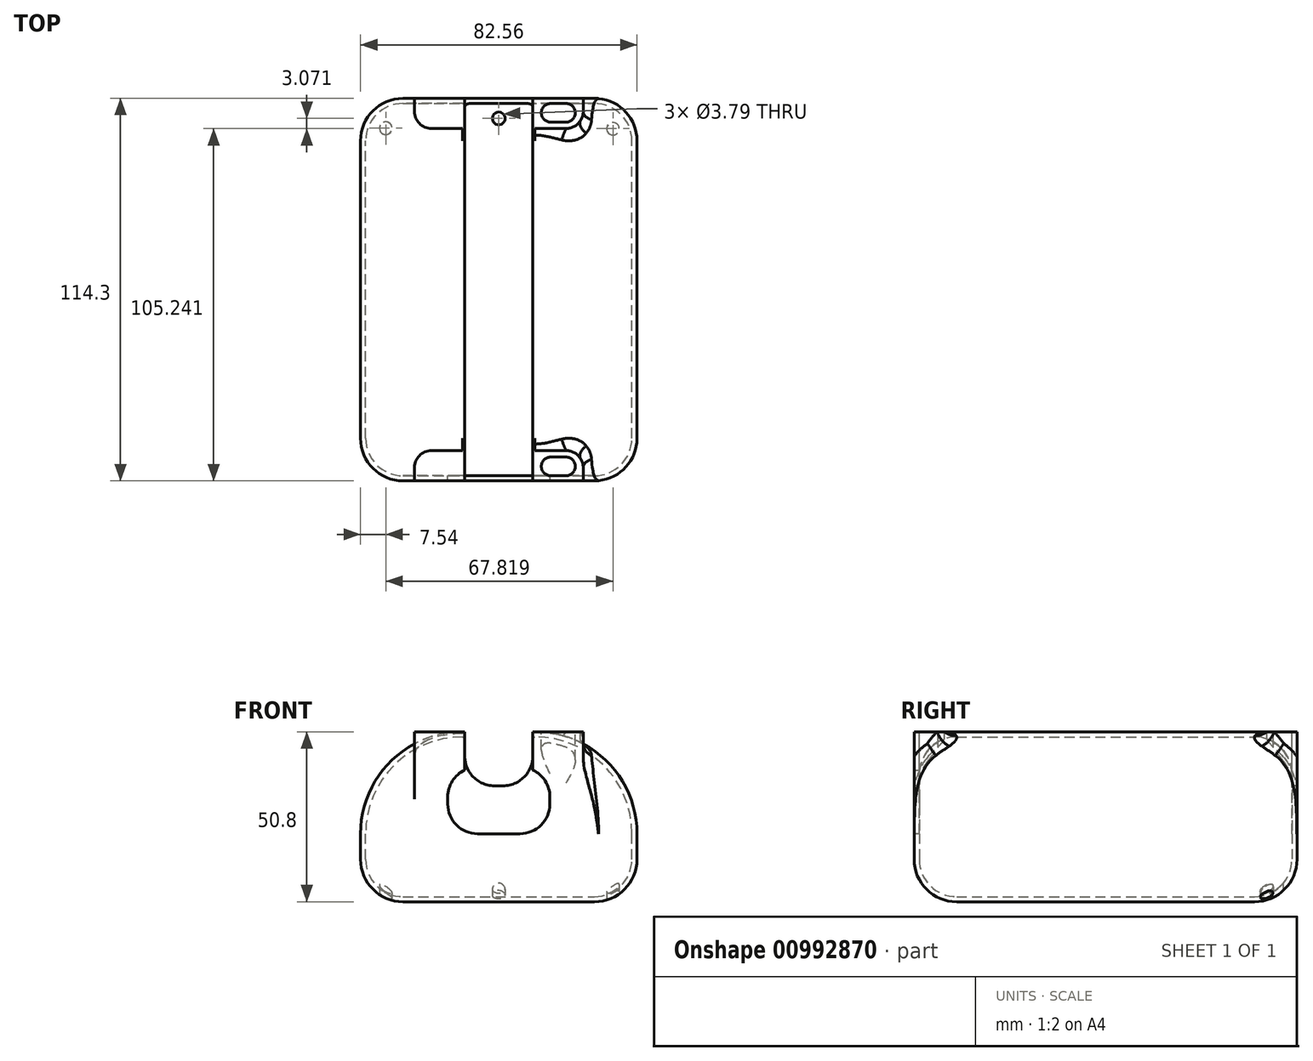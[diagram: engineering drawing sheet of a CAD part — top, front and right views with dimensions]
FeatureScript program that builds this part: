
annotation { "Feature Type Name" : "Feature", "Feature Type Description" : "" }
export const myFeature = defineFeature(function(context is Context, id is Id, definition is map)
    precondition{}
    {
        {
            var Q0;
            Q0=qCreatedBy(makeId("Top.planeOp"),FACE);
            var sketch = newSketch(context, id + "F0", { "sketchPlane" : qUnion([Q0])});
            skLineSegment(sketch, "E0.bottom", {"start": v(41.28, 0) * mm, "end": v(-41.28, 0) * mm});
            skLineSegment(sketch, "E0.top", {"start": v(41.28, 114.3) * mm, "end": v(-41.28, 114.3) * mm});
            skLineSegment(sketch, "E0.left", {"start": v(41.28, 0) * mm, "end": v(41.28, 114.3) * mm});
            skLineSegment(sketch, "E0.right", {"start": v(-41.28, 0) * mm, "end": v(-41.28, 114.3) * mm});
            skPoint(sketch, "E0.middle", {"position": v(0, 57.15) * mm});
            skSolve(sketch);
        }
        {
            var Q0;
            Q0=makeQuery(id+"F0.imprint","IMPRINT",FACE,{"disambiguationData":[TD([[makeQuery(id+"F0.imprint","IMPRINT",EDGE,{"derivedFrom":sQuery(id+"F0.wireOp",EDGE,"E0.bottom")}),-1.0]])]});
            extrude(context, id + "F1", {"entities" : qUnion([Q0]), "depth" : 50.8 * mm, "offsetDistance" : 25.4 * mm});
        }
        {
            var Q0;
            Q0=makeQuery(id+"F1.opExtrude","CAP_EDGE",EDGE,{"disambiguationData":[OSD([sQuery(id+"F0.wireOp",EDGE,"E0.left")])],"isStart":false});
            var Q1;
            Q1=makeQuery(id+"F1.opExtrude","CAP_EDGE",EDGE,{"disambiguationData":[OSD([sQuery(id+"F0.wireOp",EDGE,"E0.right")])],"isStart":false});
            fillet(context, id + "F2", {"entities" : qUnion([Q0, Q1]), "radius" : 30.48 * mm, "tangentPropagation" : true, "allowEdgeOverflow" : false});
        }
        {
            var Q0;
            Q0=makeQuery(id+"F1.opExtrude","SWEPT_FACE",FACE,{"disambiguationData":[OSD([sQuery(id+"F0.wireOp",EDGE,"E0.left")])]});
            var Q1;
            Q1=makeQuery(id+"F1.opExtrude","SWEPT_FACE",FACE,{"disambiguationData":[OSD([sQuery(id+"F0.wireOp",EDGE,"E0.right")])]});
            var Q2;
            Q2=makeQuery(id+"F1.opExtrude","CAP_EDGE",EDGE,{"disambiguationData":[OSD([sQuery(id+"F0.wireOp",EDGE,"E0.top")])],"isStart":true});
            var Q3;
            Q3=makeQuery(id+"F1.opExtrude","CAP_EDGE",EDGE,{"disambiguationData":[OSD([sQuery(id+"F0.wireOp",EDGE,"E0.bottom")])],"isStart":true});
            var Q4;
            Q4=makeQuery(id+"F1.opExtrude","CAP_EDGE",EDGE,{"disambiguationData":[OSD([sQuery(id+"F0.wireOp",EDGE,"E0.top")])],"isStart":false});
            fillet(context, id + "F3", {"entities" : qUnion([Q0, Q1, Q2, Q3, Q4]), "radius" : 12.7 * mm, "tangentPropagation" : true, "allowEdgeOverflow" : false});
        }
        {
            var Q0;
            {var subQ0=sQuery(id+"F0.wireOp",EDGE,"E0.right");var subQ1=sQuery(id+"F0.wireOp",EDGE,"E0.left");var subQ2=sQuery(id+"F0.wireOp",EDGE,"E0.top");var subQ3=sQuery(id+"F0.wireOp",EDGE,"E0.bottom");Q0=makeQuery(id+"F4FyCP3RIGp18HZ_1.splitOp","SPLIT_SURFACE_INTERSECT",FACE,{"derivedFrom":[makeQuery(id+"F3.opFillet","BLEND_FACE",FACE,{"disambiguationData":[OSD([subQ1]),TDD([makeQuery(id+"F1.opExtrude","CAP_EDGE",EDGE,{"disambiguationData":[OSD([subQ1])],"isStart":true})])]}),makeQuery(id+"F3.opFillet","BLEND_FACE",FACE,{"disambiguationData":[OSD([subQ1]),TDD([makeQuery(id+"F1.opExtrude","CAP_EDGE",EDGE,{"disambiguationData":[OSD([subQ1])],"isStart":false})])]}),makeQuery(id+"F3.opFillet","BLEND_FACE",FACE,{"disambiguationData":[OSD([subQ0]),TDD([makeQuery(id+"F1.opExtrude","CAP_EDGE",EDGE,{"disambiguationData":[OSD([subQ0])],"isStart":true})])]}),makeQuery(id+"F3.opFillet","BLEND_FACE",FACE,{"disambiguationData":[OSD([subQ0]),TDD([makeQuery(id+"F1.opExtrude","CAP_EDGE",EDGE,{"disambiguationData":[OSD([subQ0])],"isStart":false})])]}),makeQuery(id+"F1.opExtrude","CAP_FACE",FACE,{"disambiguationData":[OSD([subQ3,subQ2,subQ1,subQ0])],"isStart":true}),makeQuery(id+"F1.opExtrude","CAP_FACE",FACE,{"disambiguationData":[OSD([subQ3,subQ2,subQ1,subQ0])],"isStart":false}),makeQuery(id+"F1.opExtrude","SWEPT_FACE",FACE,{"disambiguationData":[OSD([subQ1])]}),makeQuery(id+"F1.opExtrude","SWEPT_FACE",FACE,{"disambiguationData":[OSD([subQ0])]})],"isFromBackBody":true});}
            var Q1;
            Q1=makeQuery(id+"F1.opExtrude","SWEPT_BODY",BODY,{"disambiguationData":[OSD([sQuery(id+"F0.wireOp",EDGE,"E0.bottom"),sQuery(id+"F0.wireOp",EDGE,"E0.top"),sQuery(id+"F0.wireOp",EDGE,"E0.left"),sQuery(id+"F0.wireOp",EDGE,"E0.right")])]});
            shell(context, id + "F4", {"isHollow" : true, "entities" : qUnion([Q0]), "parts" : qUnion([Q1]), "thickness" : 1.52 * mm});
        }
        {
            var Q0;
            Q0=makeQuery(id+"F4FyCP3RIGp18HZ_1.splitOp","SPLIT",FACE,{"derivedFrom":makeQuery(id+"F1.opExtrude","CAP_FACE",FACE,{"disambiguationData":[OSD([sQuery(id+"F0.wireOp",EDGE,"E0.bottom"),sQuery(id+"F0.wireOp",EDGE,"E0.top"),sQuery(id+"F0.wireOp",EDGE,"E0.left"),sQuery(id+"F0.wireOp",EDGE,"E0.right")])],"isStart":false}),"isFromBackBody":true});
            var sketch = newSketch(context, id + "F5", { "sketchPlane" : qUnion([Q0])});
            skLineSegment(sketch, "E1.bottom", {"start": v(12.7, 7.11) * mm, "end": v(22.86, 7.11) * mm});
            skLineSegment(sketch, "E1.top", {"start": v(12.7, 1.52) * mm, "end": v(22.86, 1.52) * mm});
            skLineSegment(sketch, "E1.left", {"start": v(12.7, 7.11) * mm, "end": v(12.7, 1.52) * mm});
            skLineSegment(sketch, "E1.right", {"start": v(22.86, 7.11) * mm, "end": v(22.86, 1.52) * mm});
            skSolve(sketch);
        }
        {
            var Q0;
            {var subQ0=sQuery(id+"F0.wireOp",EDGE,"E0.right");var subQ1=sQuery(id+"F0.wireOp",EDGE,"E0.left");var subQ2=sQuery(id+"F0.wireOp",EDGE,"E0.top");var subQ3=sQuery(id+"F0.wireOp",EDGE,"E0.bottom");var subQ4=makeQuery(id+"F1.opExtrude","CAP_FACE",FACE,{"disambiguationData":[OSD([subQ3,subQ2,subQ1,subQ0])],"isStart":false});var subQ5=subQ4;Q0=makeQuery(id+"F5.imprint","IMPRINT",FACE,{"disambiguationData":[TD([[makeQuery(id+"F5.imprint","IMPRINT",EDGE,{"derivedFrom":makeQuery(id+"F3.opFillet","BLEND_EDGE",EDGE,{"blendedFrom":[makeQuery(id+"F1.opExtrude","CAP_EDGE",EDGE,{"disambiguationData":[OSD([subQ3])],"isStart":false}),subQ5],"blendedInto":[subQ5]})}),1.0]])]});}
            var sketch = newSketch(context, id + "F6", { "sketchPlane" : qUnion([Q0])});
            skLineSegment(sketch, "E2.bottom", {"start": v(25.2, 0) * mm, "end": v(-25.2, 0) * mm});
            skLineSegment(sketch, "E2.top", {"start": v(25.2, 9.01) * mm, "end": v(10.8, 9.01) * mm});
            skLineSegment(sketch, "E2.left", {"start": v(25.2, 0) * mm, "end": v(25.2, 9.01) * mm});
            skLineSegment(sketch, "E2.right", {"start": v(-25.2, 0) * mm, "end": v(-25.2, 9.01) * mm});
            skPoint(sketch, "E2.middle", {"position": v(0, 4.5) * mm});
            skLineSegment(sketch, "E3.bottom", {"start": v(-10.8, 20.98) * mm, "end": v(10.8, 20.98) * mm});
            skLineSegment(sketch, "E3.left", {"start": v(-10.8, 20.98) * mm, "end": v(-10.8, 9.01) * mm});
            skLineSegment(sketch, "E3.right", {"start": v(10.8, 20.98) * mm, "end": v(10.8, 9.01) * mm});
            skLineSegment(sketch, "E4.trimOffspring", {"start": v(-10.8, 9.01) * mm, "end": v(-25.2, 9.01) * mm});
            skSolve(sketch);
        }
        {
            var Q0;
            Q0=makeQuery(id+"F6.imprint","IMPRINT",FACE,{"disambiguationData":[TD([[makeQuery(id+"F6.imprint","IMPRINT",EDGE,{"derivedFrom":sQuery(id+"F6.wireOp",EDGE,"E2.bottom")}),-1.0]])]});
            extrude(context, id + "F7", {"entities" : qUnion([Q0]), "operationType" : NewBodyOperationType.ADD, "endBound" : BoundingType.UP_TO_NEXT, "oppositeDirection" : true, "depth" : 25.4 * mm, "offsetDistance" : 25.4 * mm});
        }
        {
            var Q0;
            Q0 = qSketchRegion(id + "F5", true);
            extrude(context, id + "F8", {"entities" : qUnion([Q0]), "operationType" : NewBodyOperationType.REMOVE, "oppositeDirection" : true, "depth" : 25.4 * mm, "offsetDistance" : 25.4 * mm});
        }
        {
            var Q0;
            Q0=makeQuery(id+"F8.boolean.opBoolean","COPY",EDGE,{"derivedFrom":makeQuery(id+"F8.opExtrude","SWEPT_EDGE",EDGE,{"disambiguationData":[OSD([sQuery(id+"F5.wireOp",EDGE,"E1.bottom"),sQuery(id+"F5.wireOp",EDGE,"E1.left")])]})});
            var Q1;
            Q1=makeQuery(id+"FyfUCAUJJe16imM_1.1.F8.boolean.opBoolean","COPY",EDGE,{"derivedFrom":makeQuery(id+"FyfUCAUJJe16imM_1.1.F8.opExtrude","SWEPT_EDGE",EDGE,{"disambiguationData":[OSD([sQuery(id+"F5.wireOp",EDGE,"E1.bottom"),sQuery(id+"F5.wireOp",EDGE,"E1.right")])]})});
            var Q2;
            Q2=makeQuery(id+"FyfUCAUJJe16imM_1.1.F8.boolean.opBoolean","COPY",EDGE,{"derivedFrom":makeQuery(id+"FyfUCAUJJe16imM_1.1.F8.opExtrude","SWEPT_EDGE",EDGE,{"disambiguationData":[OSD([sQuery(id+"F5.wireOp",EDGE,"E1.top"),sQuery(id+"F5.wireOp",EDGE,"E1.right")])]})});
            var Q3;
            Q3=makeQuery(id+"F8.boolean.opBoolean","COPY",EDGE,{"derivedFrom":makeQuery(id+"F8.opExtrude","SWEPT_EDGE",EDGE,{"disambiguationData":[OSD([sQuery(id+"F5.wireOp",EDGE,"E1.top"),sQuery(id+"F5.wireOp",EDGE,"E1.left")])]})});
            var Q4;
            Q4=makeQuery(id+"F8.boolean.opBoolean","COPY",EDGE,{"derivedFrom":makeQuery(id+"F8.opExtrude","SWEPT_EDGE",EDGE,{"disambiguationData":[OSD([sQuery(id+"F5.wireOp",EDGE,"E1.top"),sQuery(id+"F5.wireOp",EDGE,"E1.right")])]})});
            var Q5;
            Q5=makeQuery(id+"FyfUCAUJJe16imM_1.1.F8.boolean.opBoolean","COPY",EDGE,{"derivedFrom":makeQuery(id+"FyfUCAUJJe16imM_1.1.F8.opExtrude","SWEPT_EDGE",EDGE,{"disambiguationData":[OSD([sQuery(id+"F5.wireOp",EDGE,"E1.top"),sQuery(id+"F5.wireOp",EDGE,"E1.left")])]})});
            var Q6;
            Q6=makeQuery(id+"FyfUCAUJJe16imM_1.1.F8.boolean.opBoolean","COPY",EDGE,{"derivedFrom":makeQuery(id+"FyfUCAUJJe16imM_1.1.F8.opExtrude","SWEPT_EDGE",EDGE,{"disambiguationData":[OSD([sQuery(id+"F5.wireOp",EDGE,"E1.bottom"),sQuery(id+"F5.wireOp",EDGE,"E1.left")])]})});
            var Q7;
            Q7=makeQuery(id+"F8.boolean.opBoolean","COPY",EDGE,{"derivedFrom":makeQuery(id+"F8.opExtrude","SWEPT_EDGE",EDGE,{"disambiguationData":[OSD([sQuery(id+"F5.wireOp",EDGE,"E1.bottom"),sQuery(id+"F5.wireOp",EDGE,"E1.right")])]})});
            fillet(context, id + "F9", {"entities" : qUnion([Q0, Q1, Q2, Q3, Q4, Q5, Q6, Q7]), "radius" : 2.8 * mm, "tangentPropagation" : true, "allowEdgeOverflow" : false});
        }
        {
            var Q0;
            Q0=qCreatedBy(makeId("Right.planeOp"),FACE);
            var sketch = newSketch(context, id + "F10", { "sketchPlane" : qUnion([Q0])});
            skLineSegment(sketch, "E5.bottom", {"start": v(57.15, 63.72) * mm, "end": v(151.06, 63.72) * mm});
            skLineSegment(sketch, "E5.top", {"start": v(57.15, -14.05) * mm, "end": v(151.06, -14.05) * mm});
            skLineSegment(sketch, "E5.left", {"start": v(57.15, 63.72) * mm, "end": v(57.15, -14.05) * mm});
            skLineSegment(sketch, "E5.right", {"start": v(151.06, 63.72) * mm, "end": v(151.06, -14.05) * mm});
            skSolve(sketch);
        }
        {
            var Q0;
            Q0 = qSketchRegion(id + "F10", true);
            extrude(context, id + "F11", {"entities" : qUnion([Q0]), "operationType" : NewBodyOperationType.REMOVE, "endBound" : BoundingType.SYMMETRIC, "oppositeDirection" : true, "depth" : 127 * mm, "offsetDistance" : 25.4 * mm});
        }
        {
            var Q0;
            Q0=makeQuery(id+"F1.opExtrude","SWEPT_BODY",BODY,{"disambiguationData":[OSD([sQuery(id+"F0.wireOp",EDGE,"E0.bottom"),sQuery(id+"F0.wireOp",EDGE,"E0.top"),sQuery(id+"F0.wireOp",EDGE,"E0.left"),sQuery(id+"F0.wireOp",EDGE,"E0.right")])]});
            var Q1;
            Q1=makeQuery(id+"F11.boolean.opBoolean","COPY",FACE,{"derivedFrom":makeQuery(id+"F11.opExtrude","SWEPT_FACE",FACE,{"disambiguationData":[OSD([sQuery(id+"F10.wireOp",EDGE,"E5.left")])]})});
            mirror(context, id + "F12", {"operationType" : NewBodyOperationType.ADD, "entities" : qUnion([Q0]), "mirrorPlane" : qUnion([Q1])});
        }
        {
            var Q0;
            Q0=qCreatedBy(makeId("Front.planeOp"),FACE);
            var sketch = newSketch(context, id + "F13", { "sketchPlane" : qUnion([Q0])});
            skLineSegment(sketch, "E6.bottom", {"start": v(15.24, 39.37) * mm, "end": v(-15.24, 39.37) * mm});
            skLineSegment(sketch, "E6.top", {"start": v(15.24, 20.32) * mm, "end": v(-15.24, 20.32) * mm});
            skLineSegment(sketch, "E6.left", {"start": v(15.24, 39.37) * mm, "end": v(15.24, 20.32) * mm});
            skLineSegment(sketch, "E6.right", {"start": v(-15.24, 39.37) * mm, "end": v(-15.24, 20.32) * mm});
            skPoint(sketch, "E6.middle", {"position": v(0, 29.85) * mm});
            skSolve(sketch);
        }
        {
            var Q0;
            Q0 = qSketchRegion(id + "F13", true);
            extrude(context, id + "F14", {"entities" : qUnion([Q0]), "operationType" : NewBodyOperationType.REMOVE, "oppositeDirection" : true, "depth" : 25.4 * mm, "offsetDistance" : 25.4 * mm});
        }
        {
            var Q0;
            Q0=qCreatedBy(makeId("Top.planeOp"),FACE);
            var sketch = newSketch(context, id + "F15", { "sketchPlane" : qUnion([Q0])});
            skCircle(sketch, "E7", {"center": v(34.08, 105.24) * mm, "radius": 1.9 * mm});
            skCircle(sketch, "E8", {"center": v(-33.74, 105.37) * mm, "radius": 1.9 * mm});
            skCircle(sketch, "E9", {"center": v(0, 108.31) * mm, "radius": 1.9 * mm});
            skSolve(sketch);
        }
        {
            var Q0;
            Q0 = qSketchRegion(id + "F15", true);
            extrude(context, id + "F16", {"entities" : qUnion([Q0]), "operationType" : NewBodyOperationType.REMOVE, "depth" : 25.4 * mm, "offsetDistance" : 25.4 * mm});
        }
        {
            var Q0;
            Q0=qCreatedBy(makeId("Front.planeOp"),FACE);
            var sketch = newSketch(context, id + "F17", { "sketchPlane" : qUnion([Q0])});
            skLineSegment(sketch, "E10.bottom", {"start": v(10.16, 34.66) * mm, "end": v(-10.16, 34.66) * mm});
            skLineSegment(sketch, "E10.top", {"start": v(10.16, 131.65) * mm, "end": v(-10.16, 131.65) * mm});
            skLineSegment(sketch, "E10.left", {"start": v(10.16, 34.66) * mm, "end": v(10.16, 131.65) * mm});
            skLineSegment(sketch, "E10.right", {"start": v(-10.16, 34.66) * mm, "end": v(-10.16, 131.65) * mm});
            skPoint(sketch, "E10.middle", {"position": v(0, 83.15) * mm});
            skSolve(sketch);
        }
        {
            var Q0;
            Q0 = qSketchRegion(id + "F17", true);
            extrude(context, id + "F18", {"entities" : qUnion([Q0]), "operationType" : NewBodyOperationType.REMOVE, "endBound" : BoundingType.THROUGH_ALL, "oppositeDirection" : true, "depth" : 25.4 * mm, "offsetDistance" : 25.4 * mm});
        }
        {
            var Q0;
            Q0=makeQuery(id+"F14.boolean.opBoolean","COPY",EDGE,{"derivedFrom":makeQuery(id+"F14.opExtrude","SWEPT_EDGE",EDGE,{"disambiguationData":[OSD([sQuery(id+"F13.wireOp",EDGE,"E6.top"),sQuery(id+"F13.wireOp",EDGE,"E6.right")])]})});
            var Q1;
            Q1=makeQuery(id+"F14.boolean.opBoolean","COPY",EDGE,{"derivedFrom":makeQuery(id+"F14.opExtrude","SWEPT_EDGE",EDGE,{"disambiguationData":[OSD([sQuery(id+"F13.wireOp",EDGE,"E6.top"),sQuery(id+"F13.wireOp",EDGE,"E6.left")])]})});
            var Q2;
            Q2=makeQuery(id+"F14.boolean.opBoolean","COPY",EDGE,{"derivedFrom":makeQuery(id+"F14.opExtrude","SWEPT_EDGE",EDGE,{"disambiguationData":[OSD([sQuery(id+"F13.wireOp",EDGE,"E6.bottom"),sQuery(id+"F13.wireOp",EDGE,"E6.right")])]})});
            var Q3;
            Q3=makeQuery(id+"F14.boolean.opBoolean","COPY",EDGE,{"derivedFrom":makeQuery(id+"F14.opExtrude","SWEPT_EDGE",EDGE,{"disambiguationData":[OSD([sQuery(id+"F13.wireOp",EDGE,"E6.bottom"),sQuery(id+"F13.wireOp",EDGE,"E6.left")])]})});
            var Q4;
            Q4=makeQuery(id+"F18.boolean.opBoolean","COPY",EDGE,{"derivedFrom":makeQuery(id+"F18.opExtrude","SWEPT_EDGE",EDGE,{"disambiguationData":[OSD([sQuery(id+"F17.wireOp",EDGE,"E10.bottom"),sQuery(id+"F17.wireOp",EDGE,"E10.right")])]})});
            var Q5;
            Q5=makeQuery(id+"F18.boolean.opBoolean","COPY",EDGE,{"derivedFrom":makeQuery(id+"F18.opExtrude","SWEPT_EDGE",EDGE,{"disambiguationData":[OSD([sQuery(id+"F17.wireOp",EDGE,"E10.bottom"),sQuery(id+"F17.wireOp",EDGE,"E10.left")])]})});
            fillet(context, id + "F19", {"entities" : qUnion([Q0, Q1, Q2, Q3, Q4, Q5]), "radius" : 8.9 * mm, "tangentPropagation" : true, "allowEdgeOverflow" : false});
        }
        {
            var Q0;
            Q0=makeQuery(id+"F7.opExtrude","SWEPT_EDGE",EDGE,{"disambiguationData":[OSD([sQuery(id+"F6.wireOp",EDGE,"E2.top"),sQuery(id+"F6.wireOp",EDGE,"E2.left")])]});
            var Q1;
            Q1=makeQuery(id+"F7.opExtrude","SWEPT_EDGE",EDGE,{"disambiguationData":[OSD([sQuery(id+"F6.wireOp",EDGE,"E2.right"),sQuery(id+"F6.wireOp",EDGE,"E4.trimOffspring")])]});
            var Q2;
            Q2=makeQuery(id+"F12.opPattern","COPY",EDGE,{"derivedFrom":makeQuery(id+"F7.opExtrude","SWEPT_EDGE",EDGE,{"disambiguationData":[OSD([sQuery(id+"F6.wireOp",EDGE,"E2.right"),sQuery(id+"F6.wireOp",EDGE,"E4.trimOffspring")])]}),"instanceName":"1"});
            var Q3;
            Q3=makeQuery(id+"F12.opPattern","COPY",EDGE,{"derivedFrom":makeQuery(id+"F7.opExtrude","SWEPT_EDGE",EDGE,{"disambiguationData":[OSD([sQuery(id+"F6.wireOp",EDGE,"E2.top"),sQuery(id+"F6.wireOp",EDGE,"E2.left")])]}),"instanceName":"1"});
            fillet(context, id + "F20", {"entities" : qUnion([Q0, Q1, Q2, Q3]), "radius" : 5.08 * mm, "tangentPropagation" : true, "allowEdgeOverflow" : false});
        }
        {
            var Q0;
            {var subQ0=sQuery(id+"F0.wireOp",EDGE,"E0.bottom");var subQ1=sQuery(id+"F0.wireOp",EDGE,"E0.left");Q0=makeQuery(id+"F20.opFillet","BLEND_EDGE",EDGE,{"blendedFrom":[makeQuery(id+"F7.opExtrude","SWEPT_EDGE",EDGE,{"disambiguationData":[OSD([sQuery(id+"F6.wireOp",EDGE,"E2.top"),sQuery(id+"F6.wireOp",EDGE,"E2.left")])]}),makeQuery(id+"F3.opFillet","BLEND_FACE",FACE,{"disambiguationData":[OSD([subQ0,subQ1]),TDD([makeQuery(id+"F2.opFillet","BLEND_EDGE",EDGE,{"blendedFrom":[makeQuery(id+"F1.opExtrude","CAP_EDGE",EDGE,{"disambiguationData":[OSD([subQ1])],"isStart":false}),makeQuery(id+"F1.opExtrude","SWEPT_FACE",FACE,{"disambiguationData":[OSD([subQ0])]})],"blendedInto":[makeQuery(id+"F1.opExtrude","SWEPT_FACE",FACE,{"disambiguationData":[OSD([subQ0])]})]})])]})],"blendedInto":[makeQuery(id+"F3.opFillet","BLEND_FACE",FACE,{"disambiguationData":[OSD([subQ0,subQ1]),TDD([makeQuery(id+"F2.opFillet","BLEND_EDGE",EDGE,{"blendedFrom":[makeQuery(id+"F1.opExtrude","CAP_EDGE",EDGE,{"disambiguationData":[OSD([subQ1])],"isStart":false}),makeQuery(id+"F1.opExtrude","SWEPT_FACE",FACE,{"disambiguationData":[OSD([subQ0])]})],"blendedInto":[makeQuery(id+"F1.opExtrude","SWEPT_FACE",FACE,{"disambiguationData":[OSD([subQ0])]})]})])]})]});}
            var Q1;
            Q1=makeQuery(id+"F7.opExtrude","CAP_EDGE",EDGE,{"disambiguationData":[OSD([sQuery(id+"F6.wireOp",EDGE,"E4.trimOffspring")])],"isStart":false});
            var Q2;
            {var subQ0=sQuery(id+"F0.wireOp",EDGE,"E0.bottom");var subQ1=sQuery(id+"F0.wireOp",EDGE,"E0.left");Q2=makeQuery(id+"F20.opFillet","BLEND_EDGE",EDGE,{"blendedFrom":[makeQuery(id+"F12.opPattern","COPY",EDGE,{"derivedFrom":makeQuery(id+"F7.opExtrude","SWEPT_EDGE",EDGE,{"disambiguationData":[OSD([sQuery(id+"F6.wireOp",EDGE,"E2.top"),sQuery(id+"F6.wireOp",EDGE,"E2.left")])]}),"instanceName":"1"}),makeQuery(id+"F12.opPattern","COPY",FACE,{"derivedFrom":makeQuery(id+"F3.opFillet","BLEND_FACE",FACE,{"disambiguationData":[OSD([subQ0,subQ1]),TDD([makeQuery(id+"F2.opFillet","BLEND_EDGE",EDGE,{"blendedFrom":[makeQuery(id+"F1.opExtrude","CAP_EDGE",EDGE,{"disambiguationData":[OSD([subQ1])],"isStart":false}),makeQuery(id+"F1.opExtrude","SWEPT_FACE",FACE,{"disambiguationData":[OSD([subQ0])]})],"blendedInto":[makeQuery(id+"F1.opExtrude","SWEPT_FACE",FACE,{"disambiguationData":[OSD([subQ0])]})]})])]}),"instanceName":"1"})],"blendedInto":[makeQuery(id+"F12.opPattern","COPY",FACE,{"derivedFrom":makeQuery(id+"F3.opFillet","BLEND_FACE",FACE,{"disambiguationData":[OSD([subQ0,subQ1]),TDD([makeQuery(id+"F2.opFillet","BLEND_EDGE",EDGE,{"blendedFrom":[makeQuery(id+"F1.opExtrude","CAP_EDGE",EDGE,{"disambiguationData":[OSD([subQ1])],"isStart":false}),makeQuery(id+"F1.opExtrude","SWEPT_FACE",FACE,{"disambiguationData":[OSD([subQ0])]})],"blendedInto":[makeQuery(id+"F1.opExtrude","SWEPT_FACE",FACE,{"disambiguationData":[OSD([subQ0])]})]})])]}),"instanceName":"1"})]});}
            var Q3;
            Q3=makeQuery(id+"F12.opPattern","COPY",EDGE,{"derivedFrom":makeQuery(id+"F7.opExtrude","CAP_EDGE",EDGE,{"disambiguationData":[OSD([sQuery(id+"F6.wireOp",EDGE,"E4.trimOffspring")])],"isStart":false}),"instanceName":"1"});
            fillet(context, id + "F21", {"entities" : qUnion([Q0, Q1, Q2, Q3]), "radius" : 5.08 * mm, "tangentPropagation" : true, "allowEdgeOverflow" : false});
        }
    });
